# Revit family: SOLA_Outdoor_Single_Sink_550mm_AU
name_source: partatom
category: Generic Models
units: mm (PartAtom-declared; Revit-internal decimal feet)

## family parameters
Always vertical = Yes
Can host rebar = No
Cut with Voids When Loaded = No
Maintain Annotation Orientation = No
OmniClass Number = 23.45.05.14.14
OmniClass Title = Sinks/Lavatories
Part Type = Normal
Room Calculation Point = No
Round Connector Dimension = Use Diameter
Shared = No
Work Plane-Based = No

## types (1)
- SOLA Outdoor Single Sink 550mm
    CW Connection = False
    Category = Kitchen Sinks
    Default Elevation = 0 mm  [stored 0 ft]
    Description = SOLA Outdoor Single Sink 550mm
    HW Connection = False
    Manufacturer = ABI Interiors Pty Ltd
    Model = Brushed Brass (15954), Brushed Copper (15955), Brushed Gunmetal (15956), Stainless Steel (15957)
    Part Number = Brushed Brass (15954), Brushed Copper (15955), Brushed Gunmetal (15956), Stainless Steel (15957)
    Title = SOLA Outdoor Single Sink 550mm
    URL = https://www.abiinteriors.com.au
    Vent Connection = False
    Volume = 0 m³
    Waste Connection = False

note: [stored X ft] marks values corroborated as IEEE doubles in the binary element streams (Revit-internal decimal feet)

## geometry (parser evidence)
native form markers: Sweep x2
no freeform markers — native parametric forms only
